# Revit family: Qf_Fisher_2600-Cv With Check Stems
name_source: partatom
category: Specialty Equipment
revit_build: Autodesk Revit 2018 (Build: 20170223_1515(x64)
units: mm (PartAtom-declared; Revit-internal decimal feet)

## family parameters
Always vertical = Yes
Cut with Voids When Loaded = No
Part Type = Normal
Room Calculation Point = No
Round Connector Dimension = Use Diameter
Shared = No
Work Plane-Based = No

## types (1)
- Qf_Fisher_2600-Cv With Check Stems
    A = 5"
    C = 3 1/2"
    Cold Water Connection Height = 0"
    Cold Water Flow = 1 GPM
    Cold Water Maximum Pressure = 200.00 psi
    Cold Water Minimum Pressure = 60.00 psi
    Cold Water RI Height = 0"
    Cold Water Size = 1"
    Cold Water Temperature Recommended = 40 °F
    Depth = 4 1/4"
    Description = CTL VLV 4BSLH RIG
    Foodservice Equipment Identifier = Yes
    Height = 3 9/16"
    Hot Water Connection Height = 0"
    Hot Water Consumption = 0 GPM
    Hot Water Flow = 1 GPM
    Hot Water Maximum Pressure = 200.00 psi
    Hot Water Minimum Pressure = 60.00 psi
    Hot Water RI Height = 0"
    Hot Water Size = 1"
    Hot Water Temperature = 160 °F
    Identify Quantity as Lot = Yes
    Length = 8"
    Manufacturer = FISHER
    Model = 2600-CV
    Weight in Pounds = 3.75

## geometry (parser evidence)
native form markers: Sweep x5
no freeform markers — native parametric forms only
